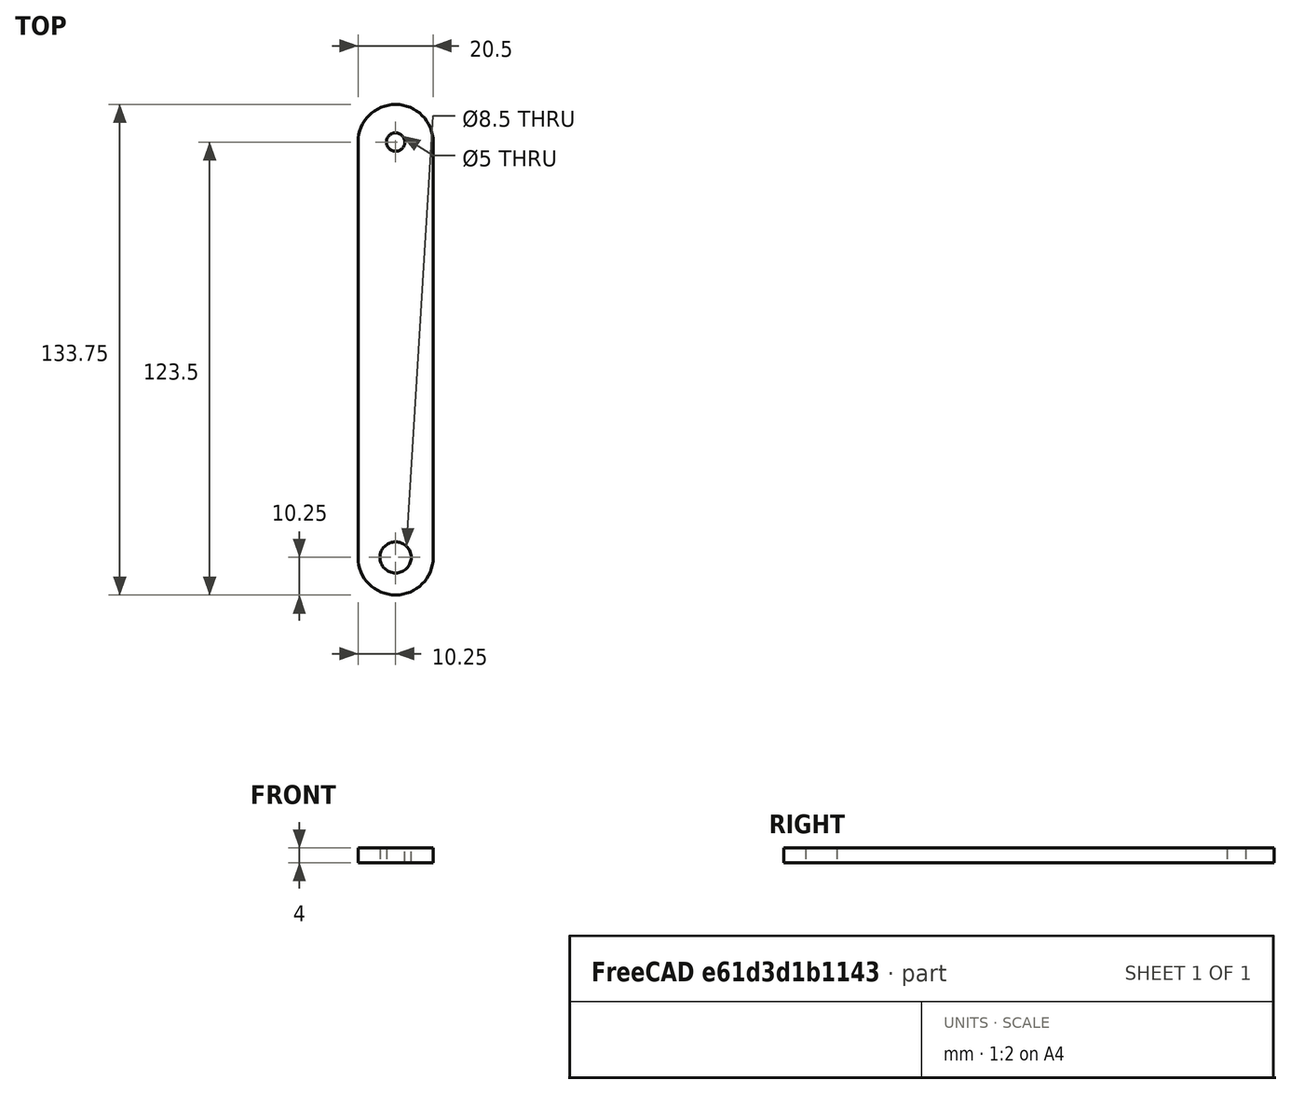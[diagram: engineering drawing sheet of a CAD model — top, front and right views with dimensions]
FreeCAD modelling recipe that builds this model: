
FCSTD DOCUMENT  (FreeCAD 0.22R37573 (Git))
Label: bike transporter tension
License: All rights reserved
LicenseURL: http://en.wikipedia.org/wiki/All_rights_reserved
objects: Sketcher::SketchObject×1, PartDesign::Pad×1, PartDesign::Body×1
note: 4 computed .brp shape members not serialized (recipe doc carries the construction recipe); baked Part::Feature solids carry a one-line shape summary decoded from their .brp

FEATURE [Sketcher::SketchObject] Sketch
  AttachmentSupport = -> [XY_Plane]
  FullyConstrained = true
  MapMode = 5
  Support = -> [XY_Plane]
  sketch-geometry (9):
    g0: Circle CenterX=0 CenterY=57.5 CenterZ=0 NormalX=0 NormalY=0 NormalZ=1 AngleXU=0 Radius=2.5
    g1: Circle CenterX=0 CenterY=-55.75 CenterZ=0 NormalX=0 NormalY=0 NormalZ=1 AngleXU=0 Radius=4.25
    g2: GeomPoint X=0 Y=60 Z=0
    g3: GeomPoint X=0 Y=-60 Z=0
    g4: ArcOfCircle CenterX=0 CenterY=57.5 CenterZ=0 NormalX=0 NormalY=0 NormalZ=1 AngleXU=0 Radius=10.25 StartAngle=5e-16 EndAngle=3.14159
    g5: ArcOfCircle CenterX=0 CenterY=-55.75 CenterZ=0 NormalX=0 NormalY=0 NormalZ=1 AngleXU=0 Radius=10.25 StartAngle=3.14159 EndAngle=6.28319
    g6: LineSegment StartX=10.25 StartY=57.5 StartZ=0 EndX=10.25 EndY=-55.75 EndZ=0
    g7: LineSegment StartX=-10.25 StartY=57.5 StartZ=0 EndX=-10.25 EndY=-55.75 EndZ=0
    g8: GeomPoint X=0 Y=-66 Z=0
  constraints (19):
    c: PointOnObject(g0,g-2)
    c: PointOnObject(g1,g-2)
    c: Diameter(g0) = 5
    c: Diameter(g1) = 8.5
    c: PointOnObject(g2,g-2)
    c: PointOnObject(g2,g0)
    c: PointOnObject(g3,g1)
    c: Symmetric(g2,g3,g-1)
    c: DistanceY(g3,g2) = 120
    c: Tangent(g4,g6) = 1.5708
    c: Tangent(g4,g7) = -1.5708
    c: Tangent(g5,g6) = 1.5708
    c: Tangent(g5,g7) = -1.5708
    c: Equal(g4,g5)
    c: Coincident(g4,g0)
    c: Coincident(g5,g1)
    c: PointOnObject(g8,g5)
    c: PointOnObject(g8,g-2)
    c: DistanceY(g8,g3) = 6
FEATURE [PartDesign::Pad] Pad
  Direction = (0,0,1)
  Length = 4
  Length2 = 10
  Profile = -> Sketch
  ReferenceAxis = -> Sketch [N_Axis]
  Suppressed = false
  Type = 0
FEATURE [PartDesign::Body] Body
  AllowCompound = false
  Group = -> [Sketch,Pad]
  Origin = -> Origin
  Tip = -> Pad
